# Revit family: Kaskad-Paralleloagram_Planter-Magnusongroup-1
name_source: partatom
category: Furniture
revit_build: Autodesk Revit 2016 (Build: 20150220_1215(x64)
units: mm (PartAtom-declared; Revit-internal decimal feet)

## family parameters
Always vertical = Yes
Cut with Voids When Loaded = No
Room Calculation Point = No
Shared = No
Work Plane-Based = No

## types (2) — shared parameters
Assembly Code = E2020200
Depth = 28 1/2"
Frame = Steel, Wrought
Glides = UHMW, Black
Heigth Plants = 15"
Keynote = 12500
Liner = UHMW, Black
Manufacturer = MAGNUSON GROUP
Type Comments = KASKAD
URL = www.magnusongroup.com
Width = 13"

## per-type parameters (varying)
| type | Cost | Description | Height |
| KAS-PS | 585 $ | Painted steel parallelogram shaped planter with liner and adjustable glides 20" height | 12" |
| KAS-PM | 765 $ | Painted steel parallelogram shaped planter with liner and adjustable glides 12" height | 20" |

note: column(s) folded — value = type name in every type: Model

## geometry (parser evidence)
native form markers: Sweep x4
no freeform markers — native parametric forms only
